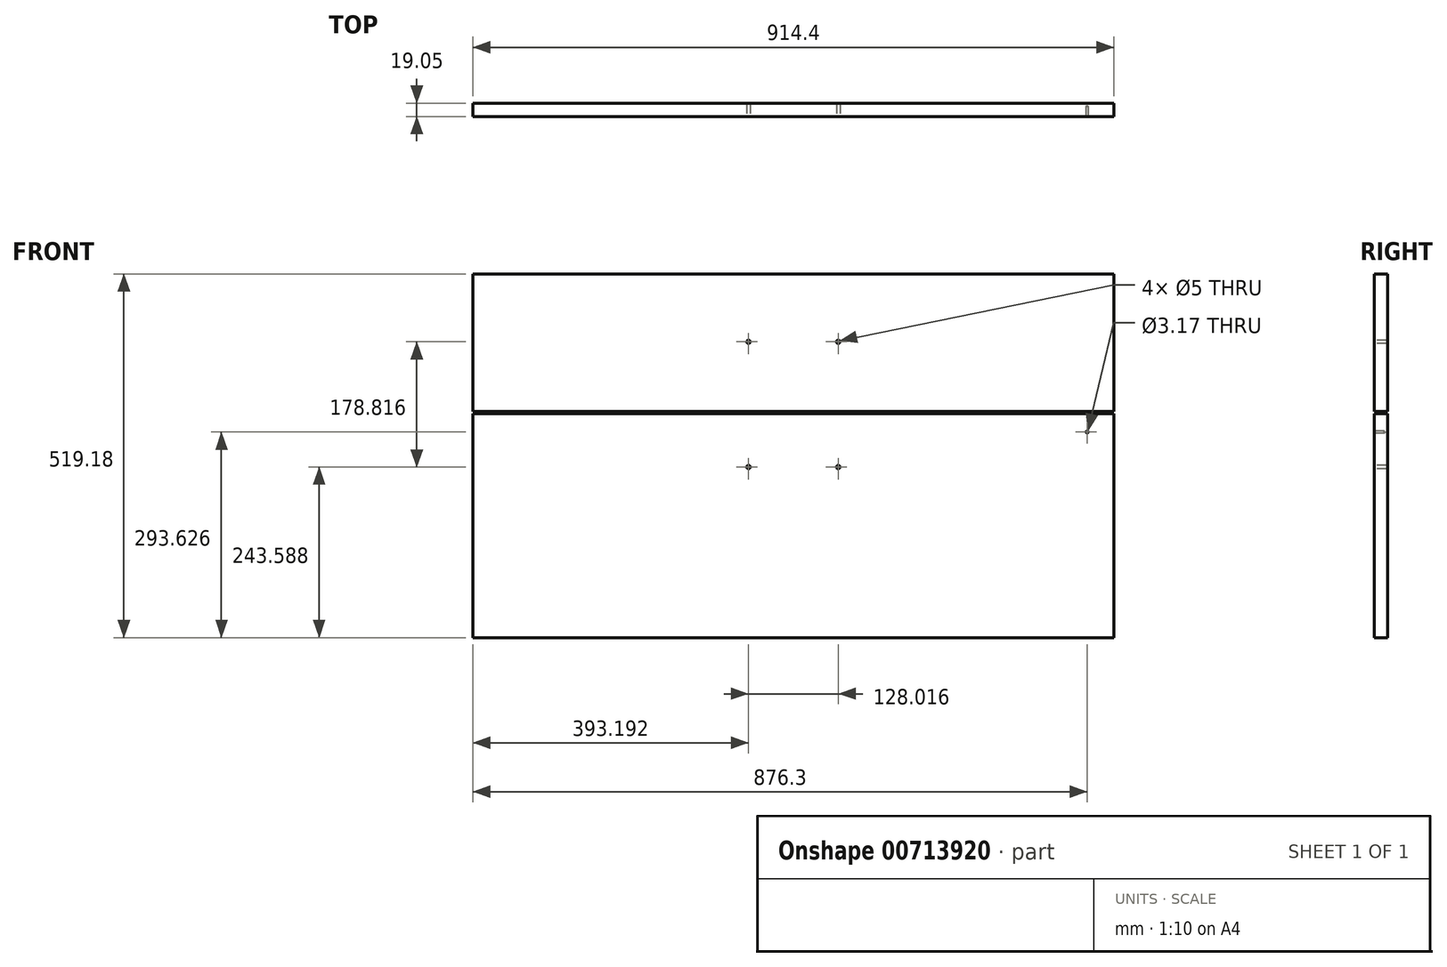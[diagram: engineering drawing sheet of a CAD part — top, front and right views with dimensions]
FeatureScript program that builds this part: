
annotation { "Feature Type Name" : "Feature", "Feature Type Description" : "" }
export const myFeature = defineFeature(function(context is Context, id is Id, definition is map)
    precondition{}
    {
        {
            var Q0;
            Q0=qCreatedBy(makeId("Front.planeOp"),FACE);
            var sketch = newSketch(context, id + "F0", { "sketchPlane" : qUnion([Q0])});
            skLineSegment(sketch, "E0.bottom", {"start": v(457.2, 259.59) * mm, "end": v(-457.2, 259.59) * mm});
            skLineSegment(sketch, "E0.top", {"start": v(457.2, -259.59) * mm, "end": v(-457.2, -259.59) * mm});
            skLineSegment(sketch, "E0.left", {"start": v(457.2, 259.59) * mm, "end": v(457.2, -259.59) * mm});
            skLineSegment(sketch, "E0.right", {"start": v(-457.2, 259.59) * mm, "end": v(-457.2, -259.59) * mm});
            skPoint(sketch, "E0.middle", {"position": v(0, 0) * mm});
            skSolve(sketch);
        }
        {
            var Q0;
            Q0=makeQuery(id+"F0.imprint","IMPRINT",FACE,{"disambiguationData":[TD([[makeQuery(id+"F0.imprint","IMPRINT",EDGE,{"derivedFrom":sQuery(id+"F0.wireOp",EDGE,"E0.bottom")}),1.0]])]});
            extrude(context, id + "F1", {"entities" : qUnion([Q0]), "depth" : 19.05 * mm, "offsetDistance" : 25.4 * mm});
        }
        {
            var Q0;
            Q0=makeQuery(id+"F1.opExtrude","CAP_FACE",FACE,{"disambiguationData":[OSD([sQuery(id+"F0.wireOp",EDGE,"E0.bottom"),sQuery(id+"F0.wireOp",EDGE,"E0.top"),sQuery(id+"F0.wireOp",EDGE,"E0.left"),sQuery(id+"F0.wireOp",EDGE,"E0.right")])],"isStart":false});
            var sketch = newSketch(context, id + "F2", { "sketchPlane" : qUnion([Q0])});
            skLineSegment(sketch, "E1", {"start": v(0, -259.59) * mm, "end": v(0, -16) * mm});
            skLineSegment(sketch, "E2", {"start": v(0, -16) * mm, "end": v(64, -16) * mm});
            skLineSegment(sketch, "E3", {"start": v(0, -16) * mm, "end": v(-64, -16) * mm});
            skLineSegment(sketch, "E4", {"start": v(0, 259.59) * mm, "end": v(0, 162.81) * mm});
            skLineSegment(sketch, "E5", {"start": v(0, 162.81) * mm, "end": v(64, 162.81) * mm});
            skLineSegment(sketch, "E6", {"start": v(0, 162.81) * mm, "end": v(-64, 162.81) * mm});
            skPoint(sketch, "E7", {"position": v(-64, -16) * mm});
            skPoint(sketch, "E8", {"position": v(64, -16) * mm});
            skPoint(sketch, "E9", {"position": v(-64, 162.81) * mm});
            skPoint(sketch, "E10", {"position": v(64, 162.81) * mm});
            skSolve(sketch);
        }
        {
            var Q0;
            Q0=sQuery(id+"F2.wireOp",VERTEX,"E9");
            var Q1;
            Q1=sQuery(id+"F2.wireOp",VERTEX,"E10");
            var Q2;
            Q2=sQuery(id+"F2.wireOp",VERTEX,"E7");
            var Q3;
            Q3=sQuery(id+"F2.wireOp",VERTEX,"E8");
            var Q4;
            Q4=makeQuery(id+"F1.opExtrude","SWEPT_BODY",BODY,{"disambiguationData":[OSD([sQuery(id+"F0.wireOp",EDGE,"E0.bottom"),sQuery(id+"F0.wireOp",EDGE,"E0.top"),sQuery(id+"F0.wireOp",EDGE,"E0.left"),sQuery(id+"F0.wireOp",EDGE,"E0.right")])]});
            hole(context, id + "F3", {"style" : HoleStyle.SIMPLE, "endStyle" : HoleEndStyle.BLIND, "holeDiameter" : 5 * mm, "majorDiameter" : 6.35 * mm, "holeDepth" : 25.4 * mm, "isTappedThrough" : true, "tappedDepth" : 12.7 * mm, "tapClearance" : 3, "startFromSketch" : true, "locations" : qUnion([Q0, Q1, Q2, Q3]), "scope" : qUnion([Q4])});
        }
        {
            var Q0;
            Q0=makeQuery(id+"F1.opExtrude","CAP_FACE",FACE,{"disambiguationData":[OSD([sQuery(id+"F0.wireOp",EDGE,"E0.bottom"),sQuery(id+"F0.wireOp",EDGE,"E0.top"),sQuery(id+"F0.wireOp",EDGE,"E0.left"),sQuery(id+"F0.wireOp",EDGE,"E0.right")])],"isStart":false});
            var sketch = newSketch(context, id + "F4", { "sketchPlane" : qUnion([Q0])});
            skLineSegment(sketch, "E11", {"start": v(457.2, -259.59) * mm, "end": v(457.2, 34.04) * mm});
            skLineSegment(sketch, "E12", {"start": v(457.2, 34.04) * mm, "end": v(419.1, 34.04) * mm});
            skPoint(sketch, "E13", {"position": v(419.1, 34.04) * mm});
            skSolve(sketch);
        }
        {
            var Q0;
            Q0=sQuery(id+"F4.wireOp",VERTEX,"E13");
            var Q1;
            Q1=makeQuery(id+"F1.opExtrude","SWEPT_BODY",BODY,{"disambiguationData":[OSD([sQuery(id+"F0.wireOp",EDGE,"E0.bottom"),sQuery(id+"F0.wireOp",EDGE,"E0.top"),sQuery(id+"F0.wireOp",EDGE,"E0.left"),sQuery(id+"F0.wireOp",EDGE,"E0.right")])]});
            hole(context, id + "F5", {"style" : HoleStyle.SIMPLE, "endStyle" : HoleEndStyle.BLIND, "holeDiameter" : 3.17 * mm, "majorDiameter" : 6.35 * mm, "holeDepth" : 14.22 * mm, "isTappedThrough" : true, "tappedDepth" : 12.7 * mm, "tapClearance" : 3, "startFromSketch" : true, "locations" : qUnion([Q0]), "scope" : qUnion([Q1])});
        }
        {
            var Q0;
            Q0=makeQuery(id+"F1.opExtrude","CAP_FACE",FACE,{"disambiguationData":[OSD([sQuery(id+"F0.wireOp",EDGE,"E0.bottom"),sQuery(id+"F0.wireOp",EDGE,"E0.top"),sQuery(id+"F0.wireOp",EDGE,"E0.left"),sQuery(id+"F0.wireOp",EDGE,"E0.right")])],"isStart":false});
            var sketch = newSketch(context, id + "F6", { "sketchPlane" : qUnion([Q0])});
            skLineSegment(sketch, "E14", {"start": v(-457.2, -259.59) * mm, "end": v(-457.2, 60.2) * mm});
            skLineSegment(sketch, "E15.bottom", {"start": v(-457.2, 60.2) * mm, "end": v(457.2, 60.2) * mm});
            skLineSegment(sketch, "E15.top", {"start": v(-457.2, 63.37) * mm, "end": v(457.2, 63.37) * mm});
            skLineSegment(sketch, "E15.left", {"start": v(-457.2, 60.2) * mm, "end": v(-457.2, 63.37) * mm});
            skLineSegment(sketch, "E15.right", {"start": v(457.2, 60.2) * mm, "end": v(457.2, 63.37) * mm});
            skSolve(sketch);
        }
        {
            var Q0;
            Q0=makeQuery(id+"F6.imprint","IMPRINT",FACE,{"disambiguationData":[TD([[makeQuery(id+"F6.imprint","IMPRINT",EDGE,{"derivedFrom":sQuery(id+"F6.wireOp",EDGE,"E15.bottom")}),1.0]])]});
            extrude(context, id + "F7", {"entities" : qUnion([Q0]), "operationType" : NewBodyOperationType.REMOVE, "oppositeDirection" : true, "depth" : 25.4 * mm, "offsetDistance" : 25.4 * mm});
        }
    });
